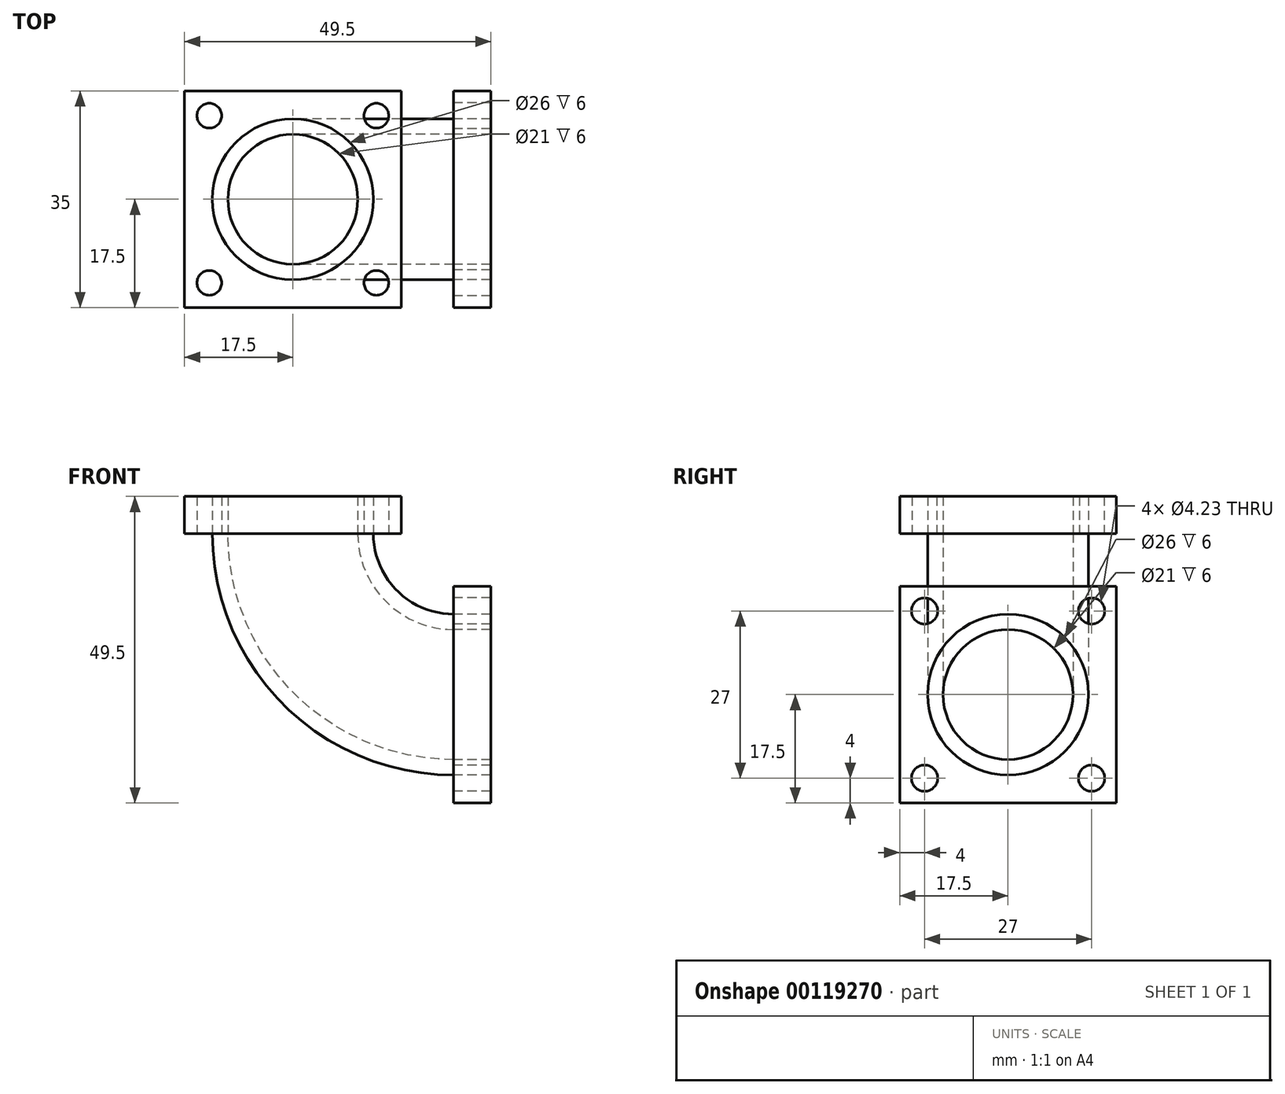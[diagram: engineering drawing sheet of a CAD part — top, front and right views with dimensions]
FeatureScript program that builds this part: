
annotation { "Feature Type Name" : "Feature", "Feature Type Description" : "" }
export const myFeature = defineFeature(function(context is Context, id is Id, definition is map)
    precondition{}
    {
        {
            var Q0;
            Q0=qCreatedBy(makeId("Front.planeOp"),FACE);
            var sketch = newSketch(context, id + "F0", { "sketchPlane" : qUnion([Q0])});
            skArc(sketch, "E0", {"start": v(-26, 0) * mm, "mid": v(-18.38, -18.38) * mm, "end": v(0, -26) * mm});
            skLineSegment(sketch, "E1", {"start": v(0, 0) * mm, "end": v(-26, 0) * mm});
            skLineSegment(sketch, "E2", {"start": v(0, 0) * mm, "end": v(0, -26) * mm});
            skSolve(sketch);
        }
        {
            var Q0;
            Q0=qCreatedBy(makeId("Top.planeOp"),FACE);
            var sketch = newSketch(context, id + "F1", { "sketchPlane" : qUnion([Q0])});
            skCircle(sketch, "E3", {"center": v(-26, 0) * mm, "radius": 13 * mm});
            skLineSegment(sketch, "E4.bottom", {"start": v(-43.5, 17.5) * mm, "end": v(-8.5, 17.5) * mm});
            skLineSegment(sketch, "E4.top", {"start": v(-43.5, -17.5) * mm, "end": v(-8.5, -17.5) * mm});
            skLineSegment(sketch, "E4.left", {"start": v(-43.5, 17.5) * mm, "end": v(-43.5, -17.5) * mm});
            skLineSegment(sketch, "E4.right", {"start": v(-8.5, 17.5) * mm, "end": v(-8.5, -17.5) * mm});
            skCircle(sketch, "E5", {"center": v(-39.5, 13.5) * mm, "radius": 2 * mm});
            skCircle(sketch, "E6.MirrorC", {"center": v(-12.5, 13.5) * mm, "radius": 2 * mm});
            skCircle(sketch, "E7.MirrorC", {"center": v(-12.5, -13.5) * mm, "radius": 2 * mm});
            skCircle(sketch, "E8.MirrorC", {"center": v(-39.5, -13.5) * mm, "radius": 2 * mm});
            skSolve(sketch);
        }
        {
            var Q0;
            Q0=qCreatedBy(makeId("Right.planeOp"),FACE);
            var sketch = newSketch(context, id + "F2", { "sketchPlane" : qUnion([Q0])});
            skCircle(sketch, "E9", {"center": v(0, -26) * mm, "radius": 13 * mm});
            skCircle(sketch, "E10", {"center": v(0, -26) * mm, "radius": 10.5 * mm});
            skLineSegment(sketch, "E11.bottom", {"start": v(-17.5, -8.5) * mm, "end": v(17.5, -8.5) * mm});
            skLineSegment(sketch, "E11.top", {"start": v(-17.5, -43.5) * mm, "end": v(17.5, -43.5) * mm});
            skLineSegment(sketch, "E11.left", {"start": v(-17.5, -8.5) * mm, "end": v(-17.5, -43.5) * mm});
            skLineSegment(sketch, "E11.right", {"start": v(17.5, -8.5) * mm, "end": v(17.5, -43.5) * mm});
            skCircle(sketch, "E12", {"center": v(-13.5, -12.5) * mm, "radius": 2.12 * mm});
            skCircle(sketch, "E13.MirrorC", {"center": v(13.5, -12.5) * mm, "radius": 2.12 * mm});
            skCircle(sketch, "E14.MirrorC", {"center": v(13.5, -39.5) * mm, "radius": 2.12 * mm});
            skCircle(sketch, "E15.MirrorC", {"center": v(-13.5, -39.5) * mm, "radius": 2.12 * mm});
            skSolve(sketch);
        }
        {
            var Q0;
            Q0=makeQuery(id+"F2.imprint","IMPRINT",FACE,{"disambiguationData":[TD([[makeQuery(id+"F2.imprint","IMPRINT",EDGE,{"derivedFrom":sQuery(id+"F2.wireOp",EDGE,"E9")}),1.0]])]});
            var Q1;
            Q1=sQuery(id+"F0.wireOp",EDGE,"E0");
            sweep(context, id + "F3", {"profiles" : qUnion([Q0]), "path" : qUnion([Q1])});
        }
        {
            var Q0;
            Q0=makeQuery(id+"F1.imprint","IMPRINT",FACE,{"disambiguationData":[TD([[makeQuery(id+"F1.imprint","IMPRINT",EDGE,{"derivedFrom":sQuery(id+"F1.wireOp",EDGE,"E3")}),-1.0]])]});
            extrude(context, id + "F4", {"entities" : qUnion([Q0]), "depth" : 6 * mm});
        }
        {
            var Q0;
            Q0=makeQuery(id+"F3.opSweep","CAP_FACE",FACE,{"disambiguationData":[OSD([sQuery(id+"F0.wireOp",VERTEX,"E0.start"),sQuery(id+"F2.wireOp",EDGE,"E9"),sQuery(id+"F2.wireOp",EDGE,"E10")])],"isStart":false});
            extrude(context, id + "F5", {"entities" : qUnion([Q0]), "depth" : 6 * mm});
        }
        {
            var Q0;
            Q0 = qSketchRegion(id + "F2", true);
            extrude(context, id + "F6", {"entities" : qUnion([Q0]), "depth" : 6 * mm});
        }
        {
            var Q0;
            Q0=makeQuery(id+"F2.imprint","IMPRINT",FACE,{"disambiguationData":[TD([[makeQuery(id+"F2.imprint","IMPRINT",EDGE,{"derivedFrom":sQuery(id+"F2.wireOp",EDGE,"E9")}),1.0]])]});
            extrude(context, id + "F7", {"entities" : qUnion([Q0]), "depth" : 6 * mm});
        }
    });
